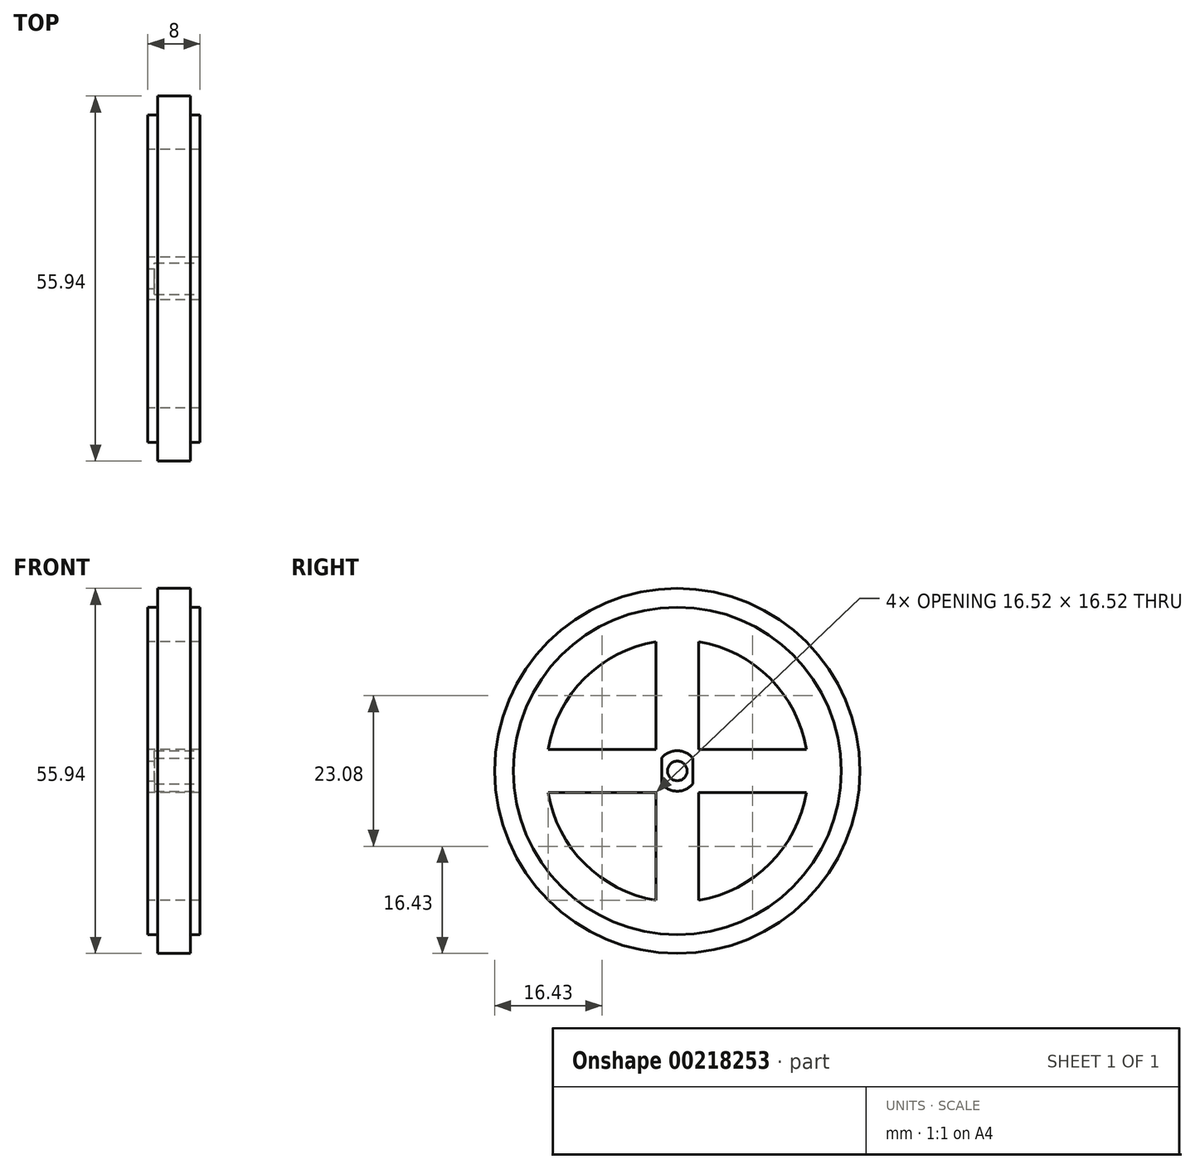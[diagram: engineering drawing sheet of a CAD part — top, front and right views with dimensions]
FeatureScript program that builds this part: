
annotation { "Feature Type Name" : "Feature", "Feature Type Description" : "" }
export const myFeature = defineFeature(function(context is Context, id is Id, definition is map)
    precondition{}
    {
        {
            var Q0;
            Q0=qCreatedBy(makeId("Right.planeOp"),FACE);
            var sketch = newSketch(context, id + "F0", { "sketchPlane" : qUnion([Q0])});
            skCircle(sketch, "E0", {"center": v(0, 0) * mm, "radius": 25.1 * mm});
            skArc(sketch, "E1", {"start": v(-3.28, 19.8) * mm, "mid": v(-14.2, 14.2) * mm, "end": v(-19.8, 3.28) * mm});
            skLineSegment(sketch, "E2", {"start": v(-3.28, 19.8) * mm, "end": v(-3.28, 3.28) * mm});
            skLineSegment(sketch, "E3", {"start": v(3.28, 19.8) * mm, "end": v(3.28, 3.28) * mm});
            skArc(sketch, "E4.trimOffspring", {"start": v(3.28, -19.8) * mm, "mid": v(14.2, -14.2) * mm, "end": v(19.8, -3.28) * mm});
            skLineSegment(sketch, "E5", {"start": v(-19.8, 3.28) * mm, "end": v(-3.28, 3.28) * mm});
            skLineSegment(sketch, "E6", {"start": v(-19.8, -3.28) * mm, "end": v(-3.28, -3.28) * mm});
            skArc(sketch, "E7.trimOffspring", {"start": v(-19.8, -3.28) * mm, "mid": v(-14.2, -14.2) * mm, "end": v(-3.28, -19.8) * mm});
            skArc(sketch, "E8.trimOffspring", {"start": v(19.8, 3.28) * mm, "mid": v(14.2, 14.2) * mm, "end": v(3.28, 19.8) * mm});
            skLineSegment(sketch, "E9.trimOffspring", {"start": v(3.28, -3.28) * mm, "end": v(19.8, -3.28) * mm});
            skLineSegment(sketch, "E10.trimOffspring", {"start": v(3.28, -3.28) * mm, "end": v(3.28, -19.8) * mm});
            skLineSegment(sketch, "E11.trimOffspring", {"start": v(3.28, 3.28) * mm, "end": v(19.8, 3.28) * mm});
            skLineSegment(sketch, "E12.trimOffspring", {"start": v(-3.28, -3.28) * mm, "end": v(-3.28, -19.8) * mm});
            skSolve(sketch);
        }
        {
            var Q0;
            Q0 = qSketchRegion(id + "F0", true);
            extrude(context, id + "F1", {"entities" : qUnion([Q0]), "depth" : 8 * mm});
        }
        {
            var Q0;
            Q0=makeQuery(id+"F1.opExtrude","CAP_FACE",FACE,{"disambiguationData":[OSD([sQuery(id+"F0.wireOp",EDGE,"E0"),sQuery(id+"F0.wireOp",EDGE,"E1"),sQuery(id+"F0.wireOp",EDGE,"E2"),sQuery(id+"F0.wireOp",EDGE,"E3"),sQuery(id+"F0.wireOp",EDGE,"E4.trimOffspring"),sQuery(id+"F0.wireOp",EDGE,"E5"),sQuery(id+"F0.wireOp",EDGE,"E6"),sQuery(id+"F0.wireOp",EDGE,"E7.trimOffspring"),sQuery(id+"F0.wireOp",EDGE,"E8.trimOffspring"),sQuery(id+"F0.wireOp",EDGE,"E9.trimOffspring"),sQuery(id+"F0.wireOp",EDGE,"E10.trimOffspring"),sQuery(id+"F0.wireOp",EDGE,"E11.trimOffspring"),sQuery(id+"F0.wireOp",EDGE,"E12.trimOffspring")])],"isStart":false});
            var sketch = newSketch(context, id + "F2", { "sketchPlane" : qUnion([Q0])});
            skArc(sketch, "E13", {"start": v(-2.4, -1.96) * mm, "mid": v(0, -3.1) * mm, "end": v(2.4, -1.96) * mm});
            skLineSegment(sketch, "E14", {"start": v(-2.4, 1.96) * mm, "end": v(-2.4, -1.96) * mm});
            skLineSegment(sketch, "E15", {"start": v(2.4, 1.96) * mm, "end": v(2.4, -1.96) * mm});
            skArc(sketch, "E16.trimOffspring", {"start": v(2.4, 1.96) * mm, "mid": v(0, 3.1) * mm, "end": v(-2.4, 1.96) * mm});
            skSolve(sketch);
        }
        {
            var Q0;
            Q0 = qSketchRegion(id + "F2", true);
            extrude(context, id + "F3", {"entities" : qUnion([Q0]), "operationType" : NewBodyOperationType.REMOVE, "oppositeDirection" : true, "depth" : 7 * mm});
        }
        {
            var Q0;
            Q0=makeQuery(id+"F3.boolean.opBoolean","COPY",FACE,{"derivedFrom":makeQuery(id+"F3.opExtrude","CAP_FACE",FACE,{"disambiguationData":[OSD([sQuery(id+"F2.wireOp",EDGE,"E13"),sQuery(id+"F2.wireOp",EDGE,"E14"),sQuery(id+"F2.wireOp",EDGE,"E15"),sQuery(id+"F2.wireOp",EDGE,"E16.trimOffspring")])],"isStart":false})});
            var sketch = newSketch(context, id + "F4", { "sketchPlane" : qUnion([Q0])});
            skCircle(sketch, "E17", {"center": v(0, 0) * mm, "radius": 1.5 * mm});
            skSolve(sketch);
        }
        {
            var Q0;
            Q0 = qSketchRegion(id + "F4", true);
            extrude(context, id + "F5", {"entities" : qUnion([Q0]), "operationType" : NewBodyOperationType.REMOVE, "oppositeDirection" : true, "depth" : 25 * mm});
        }
        {
            var Q0;
            Q0=qCreatedBy(makeId("Top.planeOp"),FACE);
            var sketch = newSketch(context, id + "F6", { "sketchPlane" : qUnion([Q0])});
            skLineSegment(sketch, "E18", {"start": v(0, 25.1) * mm, "end": v(1.5, 25.1) * mm, "construction": true});
            skPoint(sketch, "E19.end.orphan", {"position": v(0, -25.1) * mm});
            skPoint(sketch, "E19.start.orphan", {"position": v(8, -25.1) * mm});
            skLineSegment(sketch, "E20", {"start": v(1.5, 25.1) * mm, "end": v(1.5, 27.97) * mm});
            skLineSegment(sketch, "E21", {"start": v(1.5, 27.97) * mm, "end": v(6.5, 27.97) * mm});
            skLineSegment(sketch, "E22", {"start": v(6.5, 27.97) * mm, "end": v(6.5, 25.1) * mm});
            skLineSegment(sketch, "E23", {"start": v(1.5, 25.1) * mm, "end": v(6.5, 25.1) * mm});
            skLineSegment(sketch, "E24.trimOffspring", {"start": v(6.5, 25.1) * mm, "end": v(8, 25.1) * mm, "construction": true});
            skSolve(sketch);
        }
        {
            var Q0;
            Q0 = qSketchRegion(id + "F6", true);
            var Q1;
            Q1=makeQuery(id+"F1.opExtrude","CAP_EDGE",EDGE,{"disambiguationData":[OSD([sQuery(id+"F0.wireOp",EDGE,"E0")])],"isStart":false});
            revolve(context, id + "F7", {"operationType" : NewBodyOperationType.ADD, "entities" : qUnion([Q0]), "axis" : qUnion([Q1]), "revolveType" : RevolveType.FULL});
        }
    });
